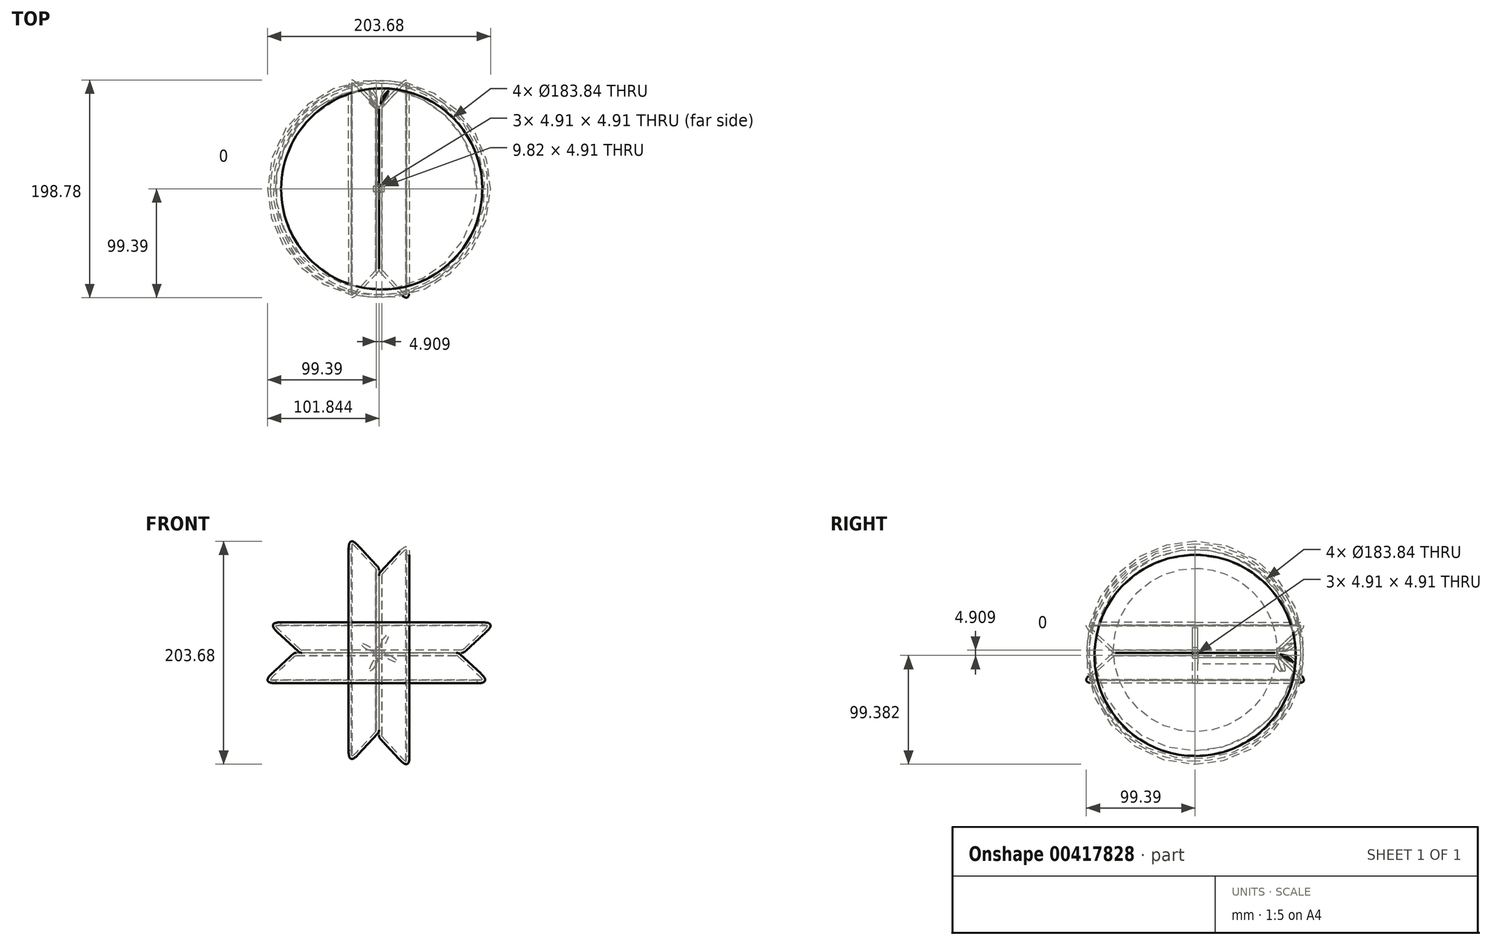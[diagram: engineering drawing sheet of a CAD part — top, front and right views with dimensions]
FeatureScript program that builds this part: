
annotation { "Feature Type Name" : "Feature", "Feature Type Description" : "" }
export const myFeature = defineFeature(function(context is Context, id is Id, definition is map)
    precondition{}
    {
        {
            var Q0;
            Q0=qCreatedBy(makeId("Right.planeOp"),FACE);
            var sketch = newSketch(context, id + "F0", { "sketchPlane" : qUnion([Q0])});
            skLineSegment(sketch, "E0", {"start": v(0, 0) * mm, "end": v(0, 27.8) * mm});
            skLineSegment(sketch, "E1", {"start": v(0, 27.8) * mm, "end": v(74.91, 27.8) * mm});
            skLineSegment(sketch, "E2", {"start": v(74.91, 27.8) * mm, "end": v(104.86, 0) * mm});
            skLineSegment(sketch, "E3", {"start": v(104.86, 0) * mm, "end": v(0, 0) * mm});
            skPoint(sketch, "E4.2.internal.snap0", {"position": v(0, 13.9) * mm});
            skSolve(sketch);
        }
        {
            var Q0;
            Q0=makeQuery(id+"F0.imprint","IMPRINT",FACE,{"disambiguationData":[TD([[makeQuery(id+"F0.imprint","IMPRINT",EDGE,{"derivedFrom":sQuery(id+"F0.wireOp",EDGE,"E0")}),-1.0]])]});
            var Q1;
            Q1=sQuery(id+"F0.wireOp",EDGE,"E0");
            revolve(context, id + "F1", {"entities" : qUnion([Q0]), "axis" : qUnion([Q1]), "revolveType" : RevolveType.FULL});
        }
        {
            var Q0;
            Q0=makeQuery(id+"F1.opRevolve","SWEPT_EDGE",EDGE,{"disambiguationData":[OSD([sQuery(id+"F0.wireOp",EDGE,"E1"),sQuery(id+"F0.wireOp",EDGE,"E2")])]});
            var Q1;
            Q1=makeQuery(id+"F1.opRevolve","SWEPT_EDGE",EDGE,{"disambiguationData":[OSD([sQuery(id+"F0.wireOp",EDGE,"E2"),sQuery(id+"F0.wireOp",EDGE,"E3")])]});
            fillet(context, id + "F2", {"entities" : qUnion([Q0, Q1]), "radius" : 5.08 * mm, "rho" : 0.5, "crossSection" : FilletCrossSection.CONIC, "allowEdgeOverflow" : false});
        }
        {
            var Q0;
            Q0=makeQuery(id+"F1.opRevolve","SWEPT_FACE",FACE,{"disambiguationData":[OSD([sQuery(id+"F0.wireOp",EDGE,"E3")])]});
            shell(context, id + "F3", {"entities" : qUnion([Q0]), "thickness" : 2.54 * mm});
        }
        {
            var Q0;
            Q0=qCreatedBy(makeId("Top.planeOp"),FACE);
            var sketch = newSketch(context, id + "F4", { "sketchPlane" : qUnion([Q0])});
            skLineSegment(sketch, "E5.bottom", {"start": v(2.45, -2.45) * mm, "end": v(-2.45, -2.45) * mm});
            skLineSegment(sketch, "E5.top", {"start": v(2.45, 2.45) * mm, "end": v(-2.45, 2.45) * mm});
            skLineSegment(sketch, "E5.left", {"start": v(2.45, -2.45) * mm, "end": v(2.45, 2.45) * mm});
            skLineSegment(sketch, "E5.right", {"start": v(-2.45, -2.45) * mm, "end": v(-2.45, 2.45) * mm});
            skPoint(sketch, "E5.middle", {"position": v(0, 0) * mm});
            skSolve(sketch);
        }
        {
            var Q0;
            Q0 = qSketchRegion(id + "F4", true);
            extrude(context, id + "F5", {"entities" : qUnion([Q0]), "operationType" : NewBodyOperationType.REMOVE, "depth" : 50.8 * mm});
        }
        {
            var Q0;
            Q0=qCreatedBy(makeId("Front.planeOp"),FACE);
            var sketch = newSketch(context, id + "F6", { "sketchPlane" : qUnion([Q0])});
            skFitSpline(sketch, "E6", {"points": [v(0, 17.87) * mm, v(-6.31, 11.2) * mm, v(0, 23.3) * mm, v(0, 17.87) * mm]});
            skSolve(sketch);
        }
        {
            var Q0;
            Q0 = qSketchRegion(id + "F6", true);
            extrude(context, id + "F7", {"entities" : qUnion([Q0]), "operationType" : NewBodyOperationType.REMOVE, "oppositeDirection" : true, "depth" : 127 * mm});
        }
        {
            var Q0;
            Q0=makeQuery(id+"F1.opRevolve","SWEPT_BODY",BODY,{"disambiguationData":[OSD([sQuery(id+"F0.wireOp",EDGE,"E0"),sQuery(id+"F0.wireOp",EDGE,"E1"),sQuery(id+"F0.wireOp",EDGE,"E2"),sQuery(id+"F0.wireOp",EDGE,"E3")])]});
            var Q1;
            Q1=makeQuery(id+"F5.boolean.opBoolean","INTERSECT",EDGE,{"derivedFrom":[makeQuery(id+"F1.opRevolve","SWEPT_FACE",FACE,{"disambiguationData":[OSD([sQuery(id+"F0.wireOp",EDGE,"E1")])]}),makeQuery(id+"F5.opExtrude","SWEPT_FACE",FACE,{"disambiguationData":[OSD([sQuery(id+"F4.wireOp",EDGE,"E5.left")])]})]});
            circularPattern(context, id + "F8", {"entities" : qUnion([Q0]), "axis" : qUnion([Q1]), "angle" : 360 * degree, "instanceCount" : 4, "equalSpace" : true});
        }
    });
